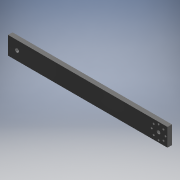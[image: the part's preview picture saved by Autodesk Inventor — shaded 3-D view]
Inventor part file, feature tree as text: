
AUTODESK INVENTOR PART (.ipt)
format: ipt  version: 2019 (Build 230136000, 136)  size: 132,608 bytes
history: native  units: mm (DEFAULTED — no unit token found)
features: extrude x4, sketch x4
ambient origin geometry x8: Origin, YZ Plane, XZ Plane, XY Plane, X Axis, Y Axis, Z Axis, Center Point
bodies: Solid1 (feature_tree)
feature tree (8):
  extrude  "Extrusion1"  Depth=25.4mm
  extrude  "Extrusion2"  Depth=6.35mm
  extrude  "Extrusion3"  Depth=25.4mm
  extrude  "Extrusion4"  Depth=25.4mm
  sketch  "Sketch1"  dims[d0=225.806mm d1=25.4mm]
  sketch  "Sketch2"  dims[d2=6.35mm d3=0.0mm d4=12.7mm]
  sketch  "Sketch3"  dims[d5=25.4mm d6=5.7658mm]
  sketch  "Sketch4"  dims[d7=2.5mm d8=0.0mm d9=25.4mm d10=12.7mm d11=12.7mm d12=5.08mm d13=10.0mm d14=0.0mm d15=12.7mm d16=19.558mm d17=7.493mm d18=2.7178mm d19=2.7178mm d20=2.7178mm d21=2.7178mm d22=2.7178mm d23=2.7178mm d24=2.7178mm d25=2.7178mm d26=25.4mm d27=0.0mm]
